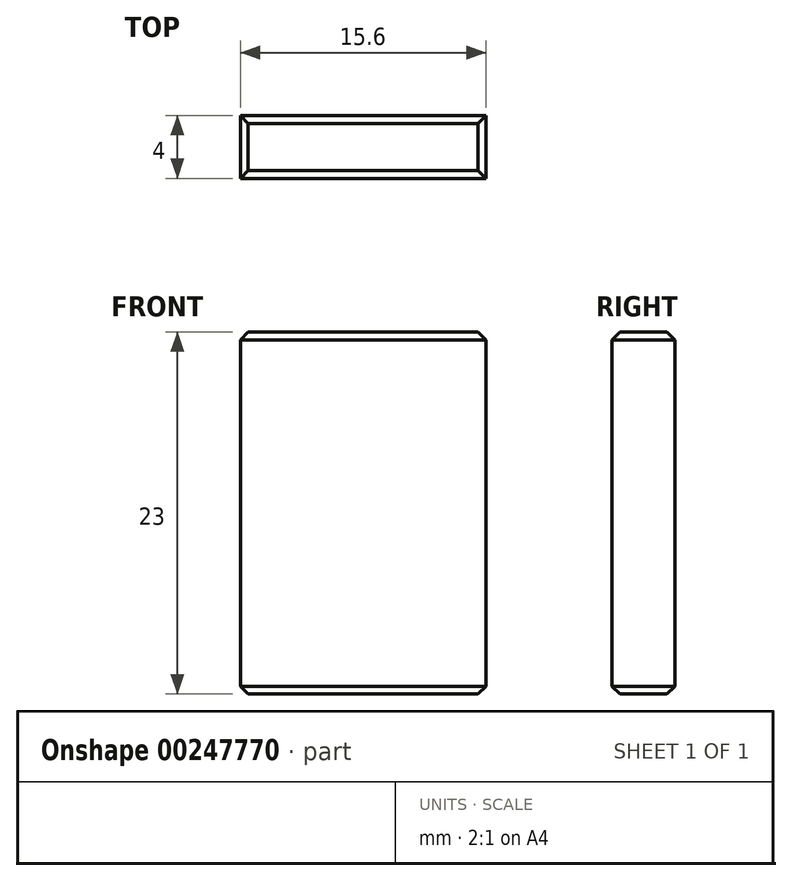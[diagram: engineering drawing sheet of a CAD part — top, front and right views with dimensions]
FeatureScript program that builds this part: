
annotation { "Feature Type Name" : "Feature", "Feature Type Description" : "" }
export const myFeature = defineFeature(function(context is Context, id is Id, definition is map)
    precondition{}
    {
        {
            var Q0;
            Q0=qCreatedBy(makeId("Front.planeOp"),FACE);
            var sketch = newSketch(context, id + "F0", { "sketchPlane" : qUnion([Q0])});
            skLineSegment(sketch, "E0", {"start": v(-7.8, 11.5) * mm, "end": v(-7.8, 0) * mm});
            skLineSegment(sketch, "E1", {"start": v(-7.8, 11.5) * mm, "end": v(0, 11.5) * mm});
            skLineSegment(sketch, "E2.MirrorCS", {"start": v(7.8, 11.5) * mm, "end": v(0, 11.5) * mm});
            skLineSegment(sketch, "E3.MirrorCS", {"start": v(7.8, 11.5) * mm, "end": v(7.8, 0) * mm});
            skLineSegment(sketch, "E4.MirrorCS", {"start": v(7.8, -11.5) * mm, "end": v(7.8, 0) * mm});
            skLineSegment(sketch, "E5.MirrorCS", {"start": v(7.8, -11.5) * mm, "end": v(0, -11.5) * mm});
            skLineSegment(sketch, "E6.MirrorCS", {"start": v(-7.8, -11.5) * mm, "end": v(0, -11.5) * mm});
            skLineSegment(sketch, "E7.MirrorCS", {"start": v(-7.8, -11.5) * mm, "end": v(-7.8, 0) * mm});
            skSolve(sketch);
        }
        {
            var Q0;
            Q0=qSketchRegion(id+"F0",true);
            extrude(context, id + "F1", {"entities" : qUnion([Q0]), "oppositeDirection" : true, "depth" : 4 * mm});
        }
        {
            var Q0;
            Q0=makeQuery(id+"F1.opExtrude","SWEPT_EDGE",EDGE,{"disambiguationData":[OSD([sQuery(id+"F0.wireOp",EDGE,"E0"),sQuery(id+"F0.wireOp",EDGE,"E1")])]});
            var Q1;
            Q1=makeQuery(id+"F1.opExtrude","CAP_EDGE",EDGE,{"disambiguationData":[OSD([sQuery(id+"F0.wireOp",EDGE,"E1"),sQuery(id+"F0.wireOp",EDGE,"E2.MirrorCS")])],"isStart":true});
            var Q2;
            Q2=makeQuery(id+"F1.opExtrude","SWEPT_EDGE",EDGE,{"disambiguationData":[OSD([sQuery(id+"F0.wireOp",EDGE,"E2.MirrorCS"),sQuery(id+"F0.wireOp",EDGE,"E3.MirrorCS")])]});
            var Q3;
            Q3=makeQuery(id+"F1.opExtrude","SWEPT_FACE",FACE,{"disambiguationData":[OSD([sQuery(id+"F0.wireOp",EDGE,"E1"),sQuery(id+"F0.wireOp",EDGE,"E2.MirrorCS")])]});
            var Q4;
            Q4=makeQuery(id+"F1.opExtrude","CAP_EDGE",EDGE,{"disambiguationData":[OSD([sQuery(id+"F0.wireOp",EDGE,"E5.MirrorCS"),sQuery(id+"F0.wireOp",EDGE,"E6.MirrorCS")])],"isStart":true});
            var Q5;
            Q5=makeQuery(id+"F1.opExtrude","SWEPT_EDGE",EDGE,{"disambiguationData":[OSD([sQuery(id+"F0.wireOp",EDGE,"E6.MirrorCS"),sQuery(id+"F0.wireOp",EDGE,"E7.MirrorCS")])]});
            var Q6;
            Q6=makeQuery(id+"F1.opExtrude","SWEPT_EDGE",EDGE,{"disambiguationData":[OSD([sQuery(id+"F0.wireOp",EDGE,"E4.MirrorCS"),sQuery(id+"F0.wireOp",EDGE,"E5.MirrorCS")])]});
            var Q7;
            Q7=makeQuery(id+"F1.opExtrude","CAP_EDGE",EDGE,{"disambiguationData":[OSD([sQuery(id+"F0.wireOp",EDGE,"E5.MirrorCS"),sQuery(id+"F0.wireOp",EDGE,"E6.MirrorCS")])],"isStart":false});
            chamfer(context, id + "F2", {"entities" : qUnion([Q0, Q1, Q2, Q3, Q4, Q5, Q6, Q7]), "width" : 0.5 * mm, "tangentPropagation" : true});
        }
    });
